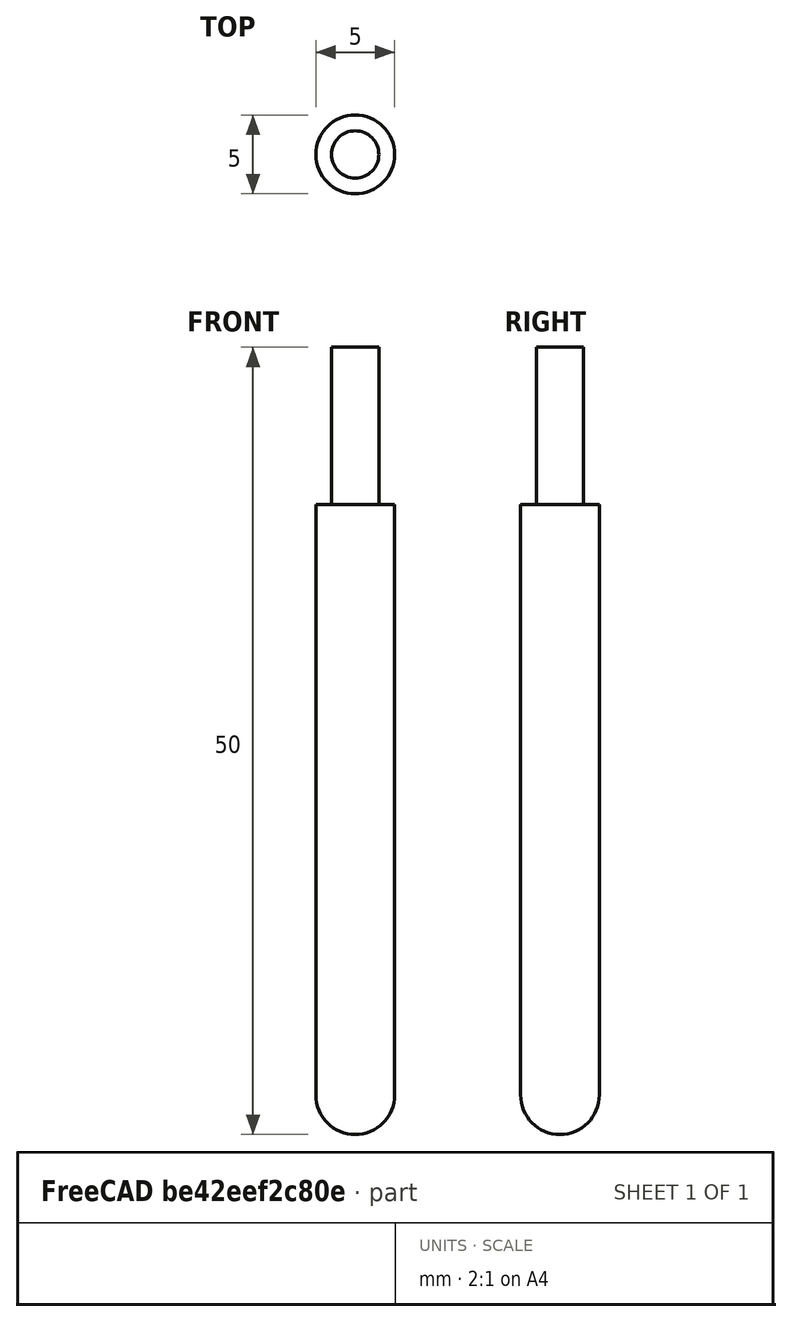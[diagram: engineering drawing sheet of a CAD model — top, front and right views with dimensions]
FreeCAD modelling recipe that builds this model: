
FCSTD DOCUMENT  (FreeCAD 0.21R32460 (Git))
Label: ballend
License: Creative Commons Attribution 4.0
LicenseURL: https://creativecommons.org/licenses/by/4.0/
objects: Sketcher::SketchObject×1, PartDesign::Revolution×1, App::FeaturePython×1, PartDesign::Body×1
note: 4 computed .brp shape members not serialized (recipe doc carries the construction recipe); baked Part::Feature solids carry a one-line shape summary decoded from their .brp

FEATURE [Sketcher::SketchObject] Sketch
  FullyConstrained = true
  MapMode = 5
  Placement = pos=(0,0,0) rot=(1,0,0;1.5708rad)
  Support = -> [XZ_Plane]
  expr: Constraints[10] = <<Attributes>>.ShankDiameter
  expr: Constraints[17] = <<Attributes>>.CuttingEdgeHeight
  expr: Constraints[3] = <<Attributes>>.Diameter
  expr: Constraints[4] = <<Attributes>>.Length
  sketch-geometry (8):
    g0: LineSegment StartX=-9e-16 StartY=50 StartZ=0 EndX=-9e-16 EndY=0 EndZ=0
    g1: LineSegment StartX=2.5 StartY=2.5 StartZ=0 EndX=2.5 EndY=40 EndZ=0
    g2: LineSegment StartX=1.5 StartY=50 StartZ=0 EndX=-9e-16 EndY=50 EndZ=0
    g3: LineSegment StartX=2.5 StartY=0 StartZ=0 EndX=-2.5 EndY=0 EndZ=0
    g4: LineSegment StartX=1.5 StartY=40.01 StartZ=0 EndX=2.5 EndY=40 EndZ=0
    g5: LineSegment StartX=1.5 StartY=50 StartZ=0 EndX=1.5 EndY=40.01 EndZ=0
    g6: LineSegment StartX=-1.5 StartY=50 StartZ=0 EndX=1.5 EndY=50 EndZ=0
    g7: ArcOfCircle CenterX=-5e-16 CenterY=2.5 CenterZ=0 NormalX=0 NormalY=0 NormalZ=1 AngleXU=0 Radius=2.5 StartAngle=4.71239 EndAngle=6.28319
  constraints (21):
    c: Vertical(g0)
    c: Vertical(g1)
    c: Horizontal(g2)
    c: DistanceX(g3,g3) = 5
    c: DistanceY(g3,g2) = 50
    c: Coincident(g1,g4)
    c: Vertical(g5)
    c: Coincident(g2,g5)
    c: Symmetric(g6,g6,g0)
    c: Coincident(g6,g2)
    c: DistanceX(g6,g6) = 3
    c: Coincident(g4,g5)
    c: Tangent(g1,g7) = -1.5708
    c: PointOnObject(g0,g3)
    c: Symmetric(g3,g3,g-2)
    c: Vertical(g3,g1)
    c: Perpendicular(g7,g0) = 4.71239
    c: DistanceY(g0,g1) = 40
    c: Coincident(g2,g0)
    c: Coincident(g0,g-1)
    c: DistanceY(g1,g4) = 0.01
FEATURE [PartDesign::Revolution] Revolution
  AllowMultiFace = false
  Angle = 360
  Axis = (0,-2e-16,1)
  Base = (0,0,0)
  Placement = pos=(0,0,0) rot=(1,0,0;1.5708rad)
  Profile = -> Sketch
  ReferenceAxis = -> Sketch [V_Axis]
  Reversed = true
FEATURE [App::FeaturePython] PropertyBag  label="Attributes"  # WARN: FeaturePython — macro-defined, semantics opaque (R4)
  Chipload = 0
  CustomPropertyGroups = Attributes | Shape
  CuttingEdgeHeight = 40
  Diameter = 5
  Flutes = 0
  Length = 50
  Material = 0
  ShankDiameter = 3
FEATURE [PartDesign::Body] Body  label="Ballend"
  Group = -> [Sketch,Revolution,PropertyBag]
  Origin = -> Origin
  Tip = -> Revolution
